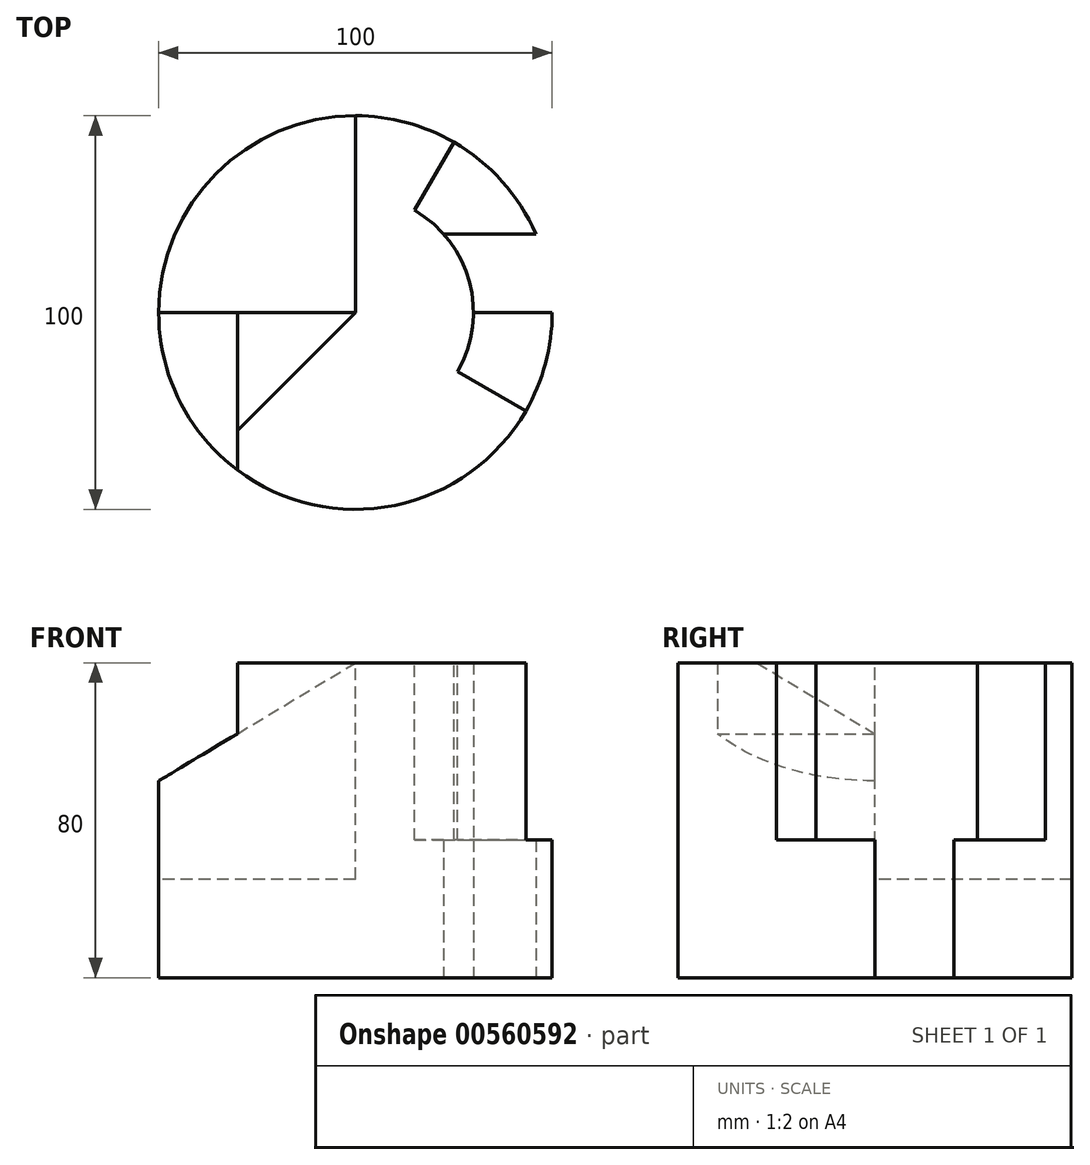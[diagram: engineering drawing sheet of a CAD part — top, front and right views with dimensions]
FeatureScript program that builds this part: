
annotation { "Feature Type Name" : "Feature", "Feature Type Description" : "" }
export const myFeature = defineFeature(function(context is Context, id is Id, definition is map)
    precondition{}
    {
        {
            var Q0;
            Q0=qCreatedBy(makeId("Top.planeOp"),FACE);
            var sketch = newSketch(context, id + "F0", { "sketchPlane" : qUnion([Q0])});
            skArc(sketch, "E0", {"start": v(45.83, 20) * mm, "mid": v(-48.95, -10.22) * mm, "end": v(50, 0) * mm});
            skArc(sketch, "E1", {"start": v(30, 0) * mm, "mid": v(28.03, 10.7) * mm, "end": v(22.36, 20) * mm});
            skLineSegment(sketch, "E2.bottom", {"start": v(30, 0) * mm, "end": v(50, 0) * mm});
            skLineSegment(sketch, "E2.top", {"start": v(22.36, 20) * mm, "end": v(45.83, 20) * mm});
            skSolve(sketch);
        }
        {
            var Q0;
            Q0 = qSketchRegion(id + "F0", true);
            extrude(context, id + "F1", {"entities" : qUnion([Q0]), "depth" : 80 * mm, "offsetDistance" : 25 * mm});
        }
        {
            var Q0;
            Q0=makeQuery(id+"F1.opExtrude","CAP_FACE",FACE,{"disambiguationData":[OSD([sQuery(id+"F0.wireOp",EDGE,"E0"),sQuery(id+"F0.wireOp",EDGE,"E1"),sQuery(id+"F0.wireOp",EDGE,"E2.bottom"),sQuery(id+"F0.wireOp",EDGE,"E2.top")])],"isStart":false});
            var sketch = newSketch(context, id + "F2", { "sketchPlane" : qUnion([Q0])});
            skLineSegment(sketch, "E3", {"start": v(0, 59.41) * mm, "end": v(0, 0) * mm});
            skLineSegment(sketch, "E4", {"start": v(0, 0) * mm, "end": v(-67.95, 0) * mm});
            skSolve(sketch);
        }
        {
            var Q0;
            {var subQ0=sQuery(id+"F2.wireOp",EDGE,"E4");var subQ1=sQuery(id+"F2.wireOp",EDGE,"E3");var subQ2=makeQuery(id+"F2.imprint","INTERSECT",VERTEX,{"derivedFrom":[subQ1,subQ0]});Q0=makeQuery(id+"F2.imprint","IMPRINT",FACE,{"disambiguationData":[TD([[makeQuery(id+"F2.imprint","IMPRINT",EDGE,{"disambiguationData":[TD([[subQ2,1.0]])],"derivedFrom":subQ1}),-1.0]])]});}
            extrude(context, id + "F3", {"entities" : qUnion([Q0]), "operationType" : NewBodyOperationType.REMOVE, "oppositeDirection" : true, "depth" : (80 - 25) * mm, "offsetDistance" : 25 * mm});
        }
        {
            var Q0;
            Q0=qCreatedBy(makeId("Front.planeOp"),FACE);
            var sketch = newSketch(context, id + "F4", { "sketchPlane" : qUnion([Q0])});
            skLineSegment(sketch, "E5", {"start": v(-30, 80) * mm, "end": v(-30, 62) * mm});
            skLineSegment(sketch, "E6", {"start": v(0, 80) * mm, "end": v(-50, 50) * mm, "construction": true});
            skLineSegment(sketch, "E7", {"start": v(-50, 50) * mm, "end": v(-30, 62) * mm});
            skLineSegment(sketch, "E8", {"start": v(-50, 50) * mm, "end": v(-67.43, 53.38) * mm});
            skLineSegment(sketch, "E9", {"start": v(-67.43, 53.38) * mm, "end": v(-55.27, 108.45) * mm});
            skLineSegment(sketch, "E10", {"start": v(-55.27, 108.45) * mm, "end": v(-30, 80) * mm});
            skSolve(sketch);
        }
        {
            var Q0;
            Q0=makeQuery(id+"F1.opExtrude","CAP_FACE",FACE,{"disambiguationData":[OSD([sQuery(id+"F0.wireOp",EDGE,"E0"),sQuery(id+"F0.wireOp",EDGE,"E1"),sQuery(id+"F0.wireOp",EDGE,"E2.bottom"),sQuery(id+"F0.wireOp",EDGE,"E2.top")])],"isStart":false});
            var sketch = newSketch(context, id + "F5", { "sketchPlane" : qUnion([Q0])});
            skLineSegment(sketch, "E11", {"start": v(15, 25.98) * mm, "end": v(38.33, 66.4) * mm});
            skLineSegment(sketch, "E12", {"start": v(25.98, -15) * mm, "end": v(46.2, -26.67) * mm});
            skArc(sketch, "E13", {"start": v(25.98, -15) * mm, "mid": v(28.98, -7.76) * mm, "end": v(30, 0) * mm});
            skLineSegment(sketch, "E14.0", {"start": v(22.36, 20) * mm, "end": v(45.83, 20) * mm});
            skLineSegment(sketch, "E15.0.0", {"start": v(50, 0) * mm, "end": v(30, 0) * mm});
            skLineSegment(sketch, "E15.0.2", {"start": v(30, 0) * mm, "end": v(50, 0) * mm});
            skArc(sketch, "E16.trimOffspring", {"start": v(22.36, 20) * mm, "mid": v(18.92, 23.28) * mm, "end": v(15, 25.98) * mm});
            skLineSegment(sketch, "E17.0.2", {"start": v(45.83, 20) * mm, "end": v(22.36, 20) * mm});
            skArc(sketch, "E18.0.0", {"start": v(-50, 0) * mm, "mid": v(-35.36, 35.36) * mm, "end": v(0, 50) * mm});
            skArc(sketch, "E18.0.2", {"start": v(0, 50) * mm, "mid": v(27.39, 41.83) * mm, "end": v(45.83, 20) * mm});
            skArc(sketch, "E18.0.4", {"start": v(45.83, 20) * mm, "mid": v(37.28, 33.32) * mm, "end": v(25, 43.3) * mm});
            skArc(sketch, "E18.0.6", {"start": v(50, 0) * mm, "mid": v(48.3, -12.94) * mm, "end": v(43.3, -25) * mm});
            skArc(sketch, "E19.0.4", {"start": v(45.83, 20) * mm, "mid": v(-48.95, -10.22) * mm, "end": v(50, 0) * mm});
            skArc(sketch, "E19.0.6", {"start": v(50, 0) * mm, "mid": v(0, -50) * mm, "end": v(-50, 0) * mm});
            skArc(sketch, "E20.trimOffspring", {"start": v(0, 50) * mm, "mid": v(-35.36, -35.36) * mm, "end": v(50, 0) * mm});
            skSolve(sketch);
        }
        {
            var Q0;
            Q0 = qSketchRegion(id + "F5", true);
            extrude(context, id + "F6", {"entities" : qUnion([Q0]), "operationType" : NewBodyOperationType.REMOVE, "oppositeDirection" : true, "depth" : (80 - 35) * mm, "offsetDistance" : 25 * mm});
        }
        {
            var Q0;
            Q0=qCreatedBy(makeId("Front.planeOp"),FACE);
            var sketch = newSketch(context, id + "F7", { "sketchPlane" : qUnion([Q0])});
            skLineSegment(sketch, "E21.0", {"start": v(0, 80) * mm, "end": v(-30, 62) * mm});
            skLineSegment(sketch, "E22.0", {"start": v(-30, 80) * mm, "end": v(-30, 62) * mm});
            skPoint(sketch, "E23.orphan", {"position": v(-50, 50) * mm});
            skSolve(sketch);
        }
        {
            var Q0;
            Q0=makeQuery(id+"F1.opExtrude","CAP_FACE",FACE,{"disambiguationData":[OSD([sQuery(id+"F0.wireOp",EDGE,"E0"),sQuery(id+"F0.wireOp",EDGE,"E1"),sQuery(id+"F0.wireOp",EDGE,"E2.bottom"),sQuery(id+"F0.wireOp",EDGE,"E2.top")])],"isStart":false});
            var sketch = newSketch(context, id + "F8", { "sketchPlane" : qUnion([Q0])});
            skLineSegment(sketch, "E24", {"start": v(0, 0) * mm, "end": v(-35.36, -35.36) * mm});
            skSolve(sketch);
        }
        {
            var Q0;
            Q0=sQuery(id+"F8.wireOp",VERTEX,"E24.start");
            var Q1;
            Q1=sQuery(id+"F8.wireOp",VERTEX,"E24.end");
            var Q2;
            Q2=sQuery(id+"F7.wireOp",VERTEX,"E23.orphan");
            cPlane(context, id + "F9", {"entities" : qUnion([Q0, Q1, Q2]), "cplaneType" : CPlaneType.THREE_POINT, "offset" : 25 * mm, "width" : 150 * mm, "height" : 150 * mm});
        }
        {
            var Q0;
            {var subQ0=sQuery(id+"F8.wireOp",EDGE,"E24");Q0=makeQuery(id+"F8.imprint","IMPRINT",FACE,{"disambiguationData":[TD([[makeQuery(id+"F8.imprint","IMPRINT",EDGE,{"derivedFrom":subQ0}),-1.0]])]});}
            var Q1;
            Q1=qCreatedBy(id+"F9.planeOp",FACE);
            extrude(context, id + "F10", {"entities" : qUnion([Q0]), "operationType" : NewBodyOperationType.REMOVE, "endBound" : BoundingType.UP_TO_SURFACE, "oppositeDirection" : true, "depth" : 25 * mm, "endBoundEntityFace" : qUnion([Q1]), "offsetDistance" : 25 * mm});
        }
        {
            var Q0;
            Q0 = qSketchRegion(id + "F4", true);
            var Q1;
            Q1=makeQuery(id+"F4.imprint","IMPRINT",FACE,{"disambiguationData":[TD([[makeQuery(id+"F4.imprint","IMPRINT",EDGE,{"derivedFrom":sQuery(id+"F4.wireOp",EDGE,"E5")}),-1.0]])]});
            extrude(context, id + "F11", {"entities" : qUnion([Q0, Q1]), "operationType" : NewBodyOperationType.REMOVE, "depth" : 124.2 * mm, "offsetDistance" : 25 * mm});
        }
    });
